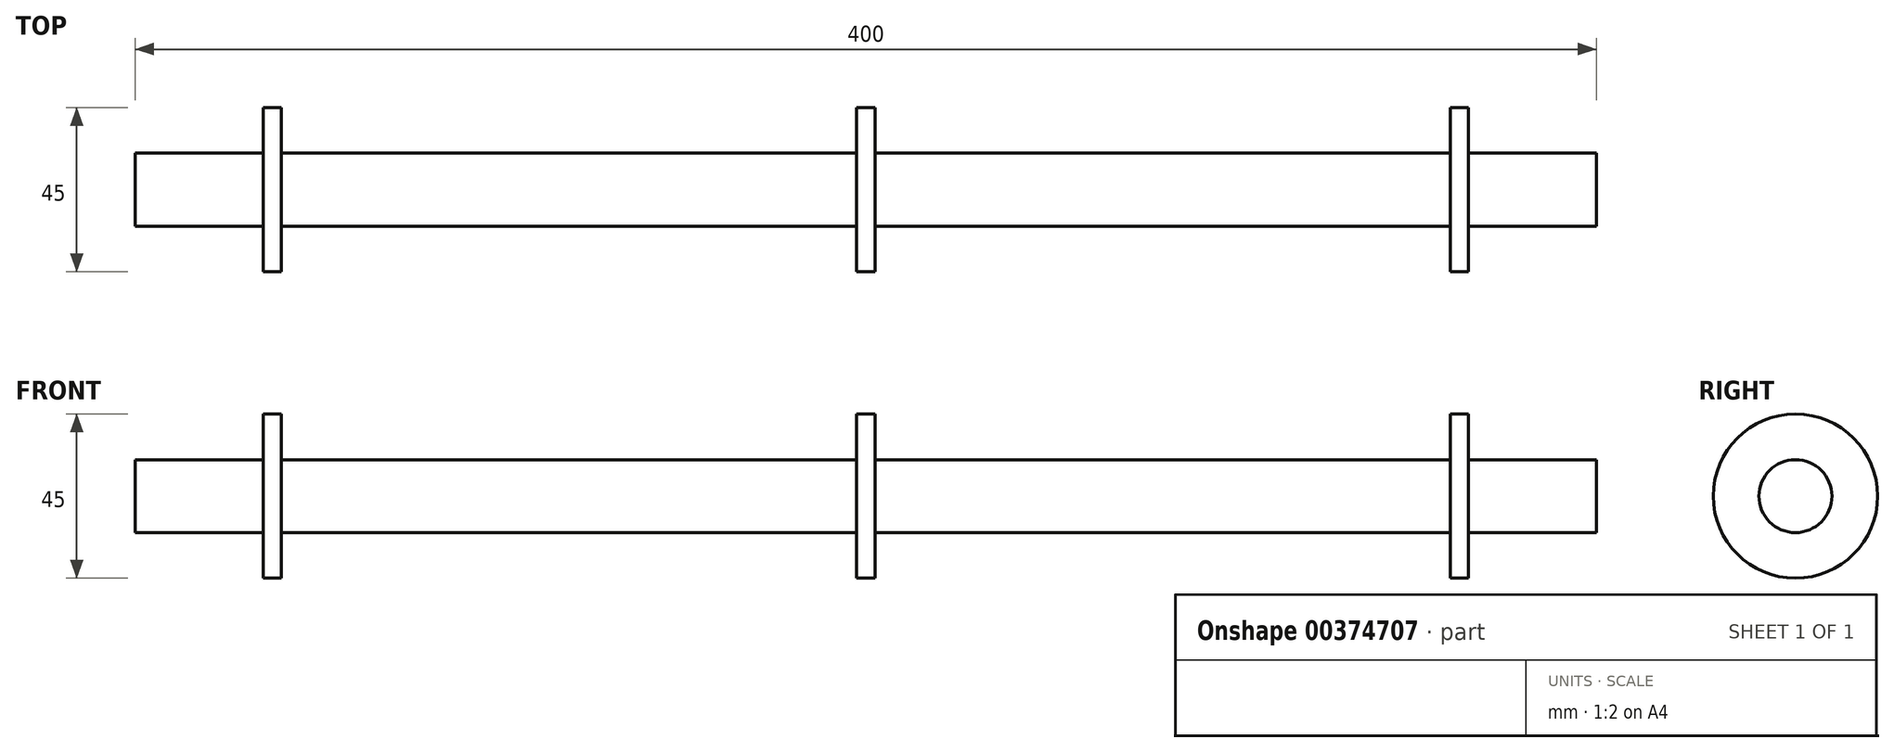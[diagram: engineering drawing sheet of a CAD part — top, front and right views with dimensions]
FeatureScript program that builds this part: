
annotation { "Feature Type Name" : "Feature", "Feature Type Description" : "" }
export const myFeature = defineFeature(function(context is Context, id is Id, definition is map)
    precondition{}
    {
        {
            var Q0;
            Q0=qCreatedBy(makeId("Right.planeOp"),FACE);
            var sketch = newSketch(context, id + "F0", { "sketchPlane" : qUnion([Q0])});
            skCircle(sketch, "E0", {"center": v(0, 0) * mm, "radius": 10 * mm});
            skSolve(sketch);
        }
        {
            var Q0;
            Q0=makeQuery(id+"F0.imprint","IMPRINT",FACE,{"disambiguationData":[TD([[makeQuery(id+"F0.imprint","IMPRINT",EDGE,{"derivedFrom":sQuery(id+"F0.wireOp",EDGE,"E0")}),1.0]])]});
            extrude(context, id + "F1", {"entities" : qUnion([Q0]), "endBound" : BoundingType.SYMMETRIC, "depth" : 400 * mm});
        }
        {
            var Q0;
            Q0=qCreatedBy(makeId("Right.planeOp"),FACE);
            cPlane(context, id + "F2", {"entities" : qUnion([Q0]), "cplaneType" : CPlaneType.OFFSET, "offset" : (330 / 2) * mm, "width" : 150 * mm, "height" : 150 * mm});
        }
        {
            var Q0;
            Q0=qCreatedBy(makeId("Right.planeOp"),FACE);
            cPlane(context, id + "F3", {"entities" : qUnion([Q0]), "cplaneType" : CPlaneType.OFFSET, "offset" : (330 / 2) * mm, "oppositeDirection" : true, "width" : 150 * mm, "height" : 150 * mm});
        }
        {
            var Q0;
            Q0=qCreatedBy(id+"F2.planeOp",FACE);
            var sketch = newSketch(context, id + "F4", { "sketchPlane" : qUnion([Q0])});
            skCircle(sketch, "E1", {"center": v(0, 0) * mm, "radius": 22.5 * mm});
            skSolve(sketch);
        }
        {
            var Q0;
            Q0 = qSketchRegion(id + "F4", true);
            extrude(context, id + "F5", {"entities" : qUnion([Q0]), "operationType" : NewBodyOperationType.ADD, "oppositeDirection" : true, "depth" : 5 * mm});
        }
        {
            var Q0;
            Q0=qCreatedBy(id+"F3.planeOp",FACE);
            var sketch = newSketch(context, id + "F6", { "sketchPlane" : qUnion([Q0])});
            skCircle(sketch, "E2", {"center": v(0, 0) * mm, "radius": 22.5 * mm});
            skSolve(sketch);
        }
        {
            var Q0;
            Q0=makeQuery(id+"F6.imprint","IMPRINT",FACE,{"disambiguationData":[TD([[makeQuery(id+"F6.imprint","IMPRINT",EDGE,{"derivedFrom":sQuery(id+"F6.wireOp",EDGE,"E2")}),1.0]])]});
            extrude(context, id + "F7", {"entities" : qUnion([Q0]), "operationType" : NewBodyOperationType.ADD, "depth" : 5 * mm});
        }
        {
            var Q0;
            Q0=qCreatedBy(makeId("Right.planeOp"),FACE);
            var sketch = newSketch(context, id + "F8", { "sketchPlane" : qUnion([Q0])});
            skCircle(sketch, "E3", {"center": v(0, 0) * mm, "radius": 22.5 * mm});
            skSolve(sketch);
        }
        {
            var Q0;
            Q0 = qSketchRegion(id + "F8", true);
            extrude(context, id + "F9", {"entities" : qUnion([Q0]), "operationType" : NewBodyOperationType.ADD, "endBound" : BoundingType.SYMMETRIC, "depth" : 5 * mm});
        }
    });
